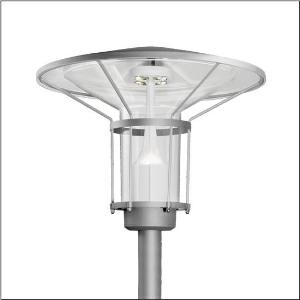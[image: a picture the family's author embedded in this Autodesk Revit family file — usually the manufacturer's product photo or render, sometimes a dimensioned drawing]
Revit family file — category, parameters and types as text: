
# Revit family: laterne_classic_iq___st1_2a_5xa5245mf14h_178e
name_source: partatom
category: Lighting Fixtures
units: mm (PartAtom-declared; Revit-internal decimal feet)

## family parameters
Cut with Voids When Loaded = No
Host = Face
Light Source = No
Part Type = Normal
Room Calculation Point = No
Round Connector Dimension = Use Diameter
Shared = No

## types (1)
- --- (1 x LED, 1380 lm, 11.8 W, 2700K)
    Apparent Load = 12 VA
    CIE Flux Codes = 21 60 93 97 100
    Color Rendering = 70
    Color Temperature = 2700K
    Default Elevation = 1800 mm
    Description = Lantern Classic iQ, mast luminaire, Module 540 iQ-SR, primary light control with 3 zone facetted reflector, of plastic, silver coated, highly specular, structured, primary optical cover: cover, of PMMA, transparent, light distribution: ST1.2a, light emission: direct distribution, primary light characteristic: asymmetric, installation type: post-top, LED, High Power LED, rated luminous flux: 1.380lm, luminous efficacy: 117lm/W, light colour: 727, colour temperature: 2700K, control gear: ECG iQ, control: pre-setting: logarithmic dimming characteristic, Street-Remote, Auto-Match, Temp-Guard, Lumen-Switch, Night-Set, Smart-Wire, Light-Fading, Desk-Remote (wireless, voltage-free reading and setting of iQ features in the workshop via application-optimized NFC function/RFID function), optimised constant luminous flux control (CLO 2.0), with terminal, 6-pole, max. 2.5mm², mains connection: 230..240V, AC, 50/60Hz, start of lifetime: 12W, end of service life: 12W, reduction: 6W, luminaire housing, upper part, of glass-fibre reinforced polyester, coated, Siteco® metallic grey (DB 702S), diameter: 750mm, height: 596mm, spigot size: d x l = 76 x 70mm (post-top) | with reducer (optional accessory) 60 x 70mm, post-top mast mounting element, of diecast aluminium, coated, Siteco® metallic grey (DB 702S), Module 540 iQ-SR, traffic white (RAL 9016), equipment: standard, protection rating (complete): IP65, insulation class (complete): insulation class II (safety insulation), certification: CE, ENEC, VDE, packaging unit: 1 piece

Light Distribution: ST1.2a
    Height = 596 mm
    Lamp = 1 x LED
    Lamp Light Flux = 1380 lm
    Lamp Power = 11.8 W
    Lamp count = 1
    Length = 750 mm
    Luminous efficacy = 117 lm/W
    Manufacturer = Siteco
    ModVariant = No
    Model = 5XA5245MF14H
    Number of Poles = 1
    OnlyDefault = Yes
    Power Factor = 1
    Product Name = Laterne Classic iQ | ST1.2a
    Product group = mast luminaire | pylon top
    ProductGroupID = 6100
    Protection Class = Protection class II
    Protection Degree = IP 65
    RLX_Detail_Level = 1
    RLX_Emergency_Light_Flux = 0 lm
    RLX_Emergency_Type = 0
    RLX_Emergency_Type_DB = No
    RlxData = <blob elided: 91521 chars, md5=31f3fe7e>
    Socket = socket
    Standby Power = 0 W
    System Light Flux = 1380 lm
    System Power = 12 W
    Type Comments = factory setting: luminous flux: 100 % | dim-lin: 254 | 472 mA
    Type Image = l_1006052.jpg
    URL = http://relux.com
    VarID = @adj_123715
    Voltage = 0 V
    Weight = 0.00 kg
    Width = 0 mm  [stored 0 ft]

note: [stored X ft] marks values corroborated as IEEE doubles in the binary element streams (Revit-internal decimal feet)

## geometry (parser evidence)
native form markers: Blend x4, Sweep x11
no freeform markers — native parametric forms only
